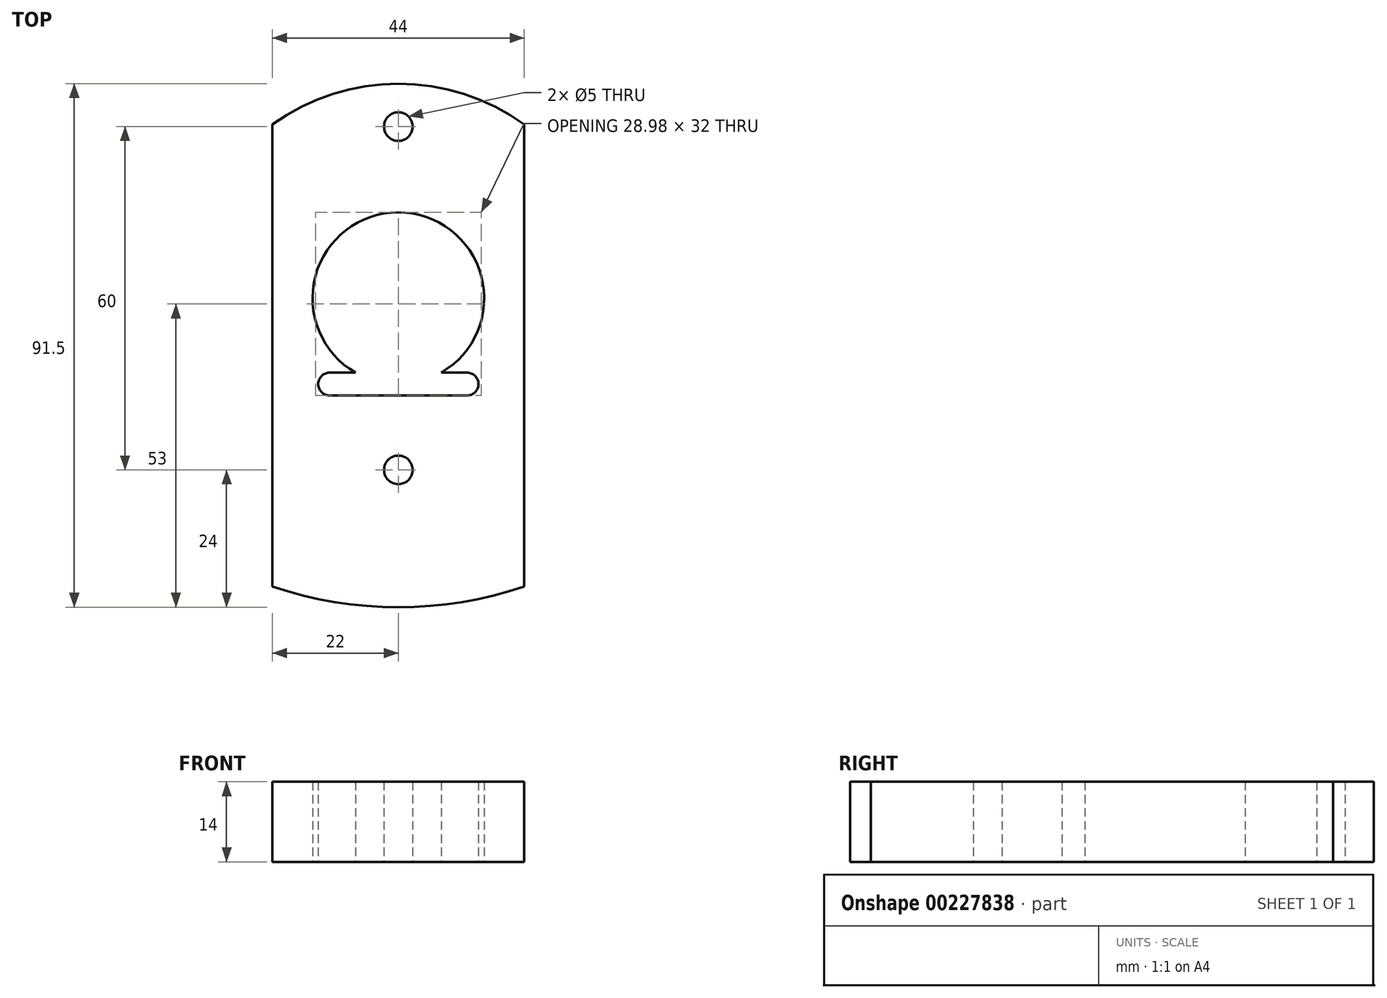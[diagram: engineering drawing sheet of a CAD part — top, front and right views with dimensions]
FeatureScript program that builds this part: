
annotation { "Feature Type Name" : "Feature", "Feature Type Description" : "" }
export const myFeature = defineFeature(function(context is Context, id is Id, definition is map)
    precondition{}
    {
        {
            var Q0;
            Q0=qCreatedBy(makeId("Top.planeOp"),FACE);
            var sketch = newSketch(context, id + "F0", { "sketchPlane" : qUnion([Q0])});
            skLineSegment(sketch, "E0", {"start": v(-22, 30.37) * mm, "end": v(-22, -50.4) * mm});
            skArc(sketch, "E1", {"start": v(-22.1, -50.37) * mm, "mid": v(0, -54) * mm, "end": v(22.1, -50.37) * mm});
            skLineSegment(sketch, "E2.MirrorCS", {"start": v(22, 30.37) * mm, "end": v(22, -50.4) * mm});
            skCircle(sketch, "E3", {"center": v(0, -30) * mm, "radius": 2.5 * mm});
            skCircle(sketch, "E4", {"center": v(0, 15) * mm, "radius": 55 * mm, "construction": true});
            skCircle(sketch, "E5", {"center": v(-15, -25) * mm, "radius": 2.5 * mm, "construction": true});
            skCircle(sketch, "E6.MirrorC", {"center": v(15, -25) * mm, "radius": 2.5 * mm, "construction": true});
            skCircle(sketch, "E7", {"center": v(0, 0) * mm, "radius": 23.5 * mm, "construction": true});
            skLineSegment(sketch, "E8", {"start": v(0, 15) * mm, "end": v(59.96, -19.62) * mm});
            skCircle(sketch, "E9", {"center": v(0, 15) * mm, "radius": 50 * mm, "construction": true});
            skCircle(sketch, "E10", {"center": v(43.3, -10) * mm, "radius": 20 * mm, "construction": true});
            skCircle(sketch, "E11", {"center": v(0, 65) * mm, "radius": 20 * mm, "construction": true});
            skCircle(sketch, "E12.MirrorC", {"center": v(-15, 25) * mm, "radius": 2.5 * mm, "construction": true});
            skCircle(sketch, "E13.MirrorC", {"center": v(15, 25) * mm, "radius": 2.5 * mm, "construction": true});
            skCircle(sketch, "E14.MirrorC", {"center": v(0, 30) * mm, "radius": 2.5 * mm});
            skArc(sketch, "E15.trimOffspring", {"start": v(22, 30.37) * mm, "mid": v(0, 37.5) * mm, "end": v(-22, 30.37) * mm});
            skCircle(sketch, "E16", {"center": v(0, 0) * mm, "radius": 15 * mm});
            skSolve(sketch);
        }
        {
            var Q0;
            Q0=qSketchRegion(id+"F0",true);
            extrude(context, id + "F1", {"entities" : qUnion([Q0]), "depth" : 7 * mm, "hasSecondDirection" : true, "secondDirectionOppositeDirection" : true, "secondDirectionDepth" : 7 * mm});
        }
        {
            var Q0;
            Q0=qCreatedBy(makeId("Top.planeOp"),FACE);
            var sketch = newSketch(context, id + "F2", { "sketchPlane" : qUnion([Q0])});
            skCircle(sketch, "E17", {"center": v(0, 0) * mm, "radius": 12.5 * mm, "construction": true});
            skLineSegment(sketch, "E18", {"start": v(-33.6, -12.5) * mm, "end": v(32.1, -12.5) * mm, "construction": true});
            skLineSegment(sketch, "E19", {"start": v(-12, -13) * mm, "end": v(0, -13) * mm});
            skLineSegment(sketch, "E20", {"start": v(0, -17) * mm, "end": v(-12, -17) * mm});
            skLineSegment(sketch, "E21", {"start": v(-12, -4.63) * mm, "end": v(-12, -31.33) * mm, "construction": true});
            skLineSegment(sketch, "E22", {"start": v(-25.25, -15) * mm, "end": v(7.52, -15) * mm, "construction": true});
            skArc(sketch, "E23", {"start": v(-12, -13) * mm, "mid": v(-14, -15) * mm, "end": v(-12, -17) * mm});
            skLineSegment(sketch, "E24.MirrorCS", {"start": v(12, -13) * mm, "end": v(0, -13) * mm});
            skLineSegment(sketch, "E25.MirrorCS", {"start": v(0, -17) * mm, "end": v(12, -17) * mm});
            skArc(sketch, "E26.MirrorCS", {"start": v(12, -13) * mm, "mid": v(14, -15) * mm, "end": v(12, -17) * mm});
            skSolve(sketch);
        }
        {
            var Q0;
            Q0 = qSketchRegion(id + "F2", true);
            extrude(context, id + "F3", {"entities" : qUnion([Q0]), "operationType" : NewBodyOperationType.REMOVE, "depth" : 25 * mm, "hasSecondDirection" : true, "secondDirectionOppositeDirection" : true, "secondDirectionDepth" : 25 * mm});
        }
    });
